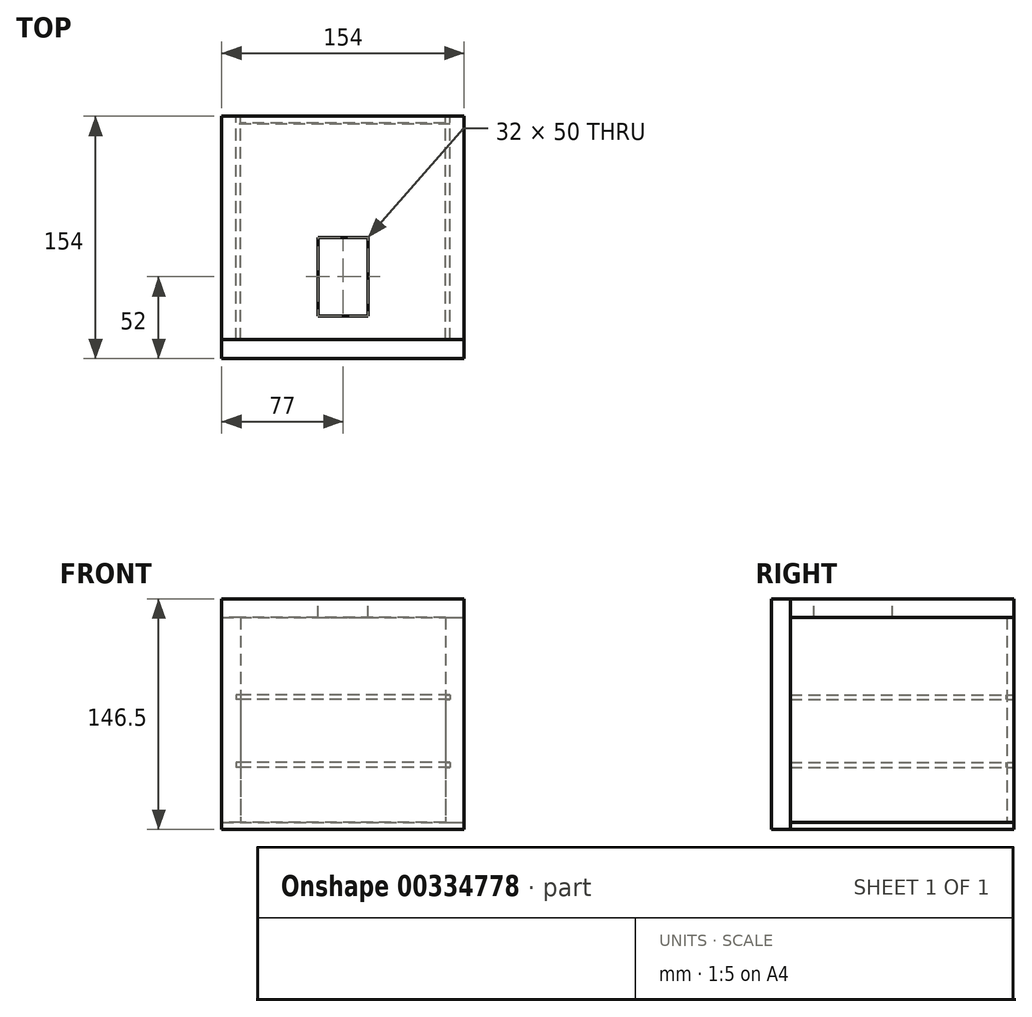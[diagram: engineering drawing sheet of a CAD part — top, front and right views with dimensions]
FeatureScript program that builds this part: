
annotation { "Feature Type Name" : "Feature", "Feature Type Description" : "" }
export const myFeature = defineFeature(function(context is Context, id is Id, definition is map)
    precondition{}
    {
        {
            var Q0;
            Q0=qCreatedBy(makeId("Front.planeOp"),FACE);
            var sketch = newSketch(context, id + "F0", { "sketchPlane" : qUnion([Q0])});
            skLineSegment(sketch, "E0.bottom", {"start": v(-77, 77) * mm, "end": v(77, 77) * mm});
            skLineSegment(sketch, "E0.top", {"start": v(-77, -69.5) * mm, "end": v(77, -69.5) * mm});
            skLineSegment(sketch, "E0.left", {"start": v(-77, 77) * mm, "end": v(-77, -69.5) * mm});
            skLineSegment(sketch, "E0.right", {"start": v(77, 77) * mm, "end": v(77, -69.5) * mm});
            skSolve(sketch);
        }
        {
            var Q0;
            Q0 = qSketchRegion(id + "F0", true);
            var Q1;
            Q1=makeQuery(id+"F0.imprint","IMPRINT",FACE,{"disambiguationData":[TD([[makeQuery(id+"F0.imprint","IMPRINT",EDGE,{"derivedFrom":sQuery(id+"F0.wireOp",EDGE,"E0.bottom")}),-1.0]])]});
            extrude(context, id + "F1", {"entities" : qUnion([Q0, Q1]), "depth" : 12 * mm});
        }
        {
            var Q0;
            Q0=makeQuery(id+"F1.opExtrude","SWEPT_FACE",FACE,{"disambiguationData":[OSD([sQuery(id+"F0.wireOp",EDGE,"E0.right")])]});
            var sketch = newSketch(context, id + "F2", { "sketchPlane" : qUnion([Q0])});
            skLineSegment(sketch, "E1.bottom", {"start": v(0, 65) * mm, "end": v(142, 65) * mm});
            skLineSegment(sketch, "E1.top", {"start": v(0, -65) * mm, "end": v(142, -65) * mm});
            skLineSegment(sketch, "E1.left", {"start": v(0, 65) * mm, "end": v(0, -65) * mm});
            skLineSegment(sketch, "E1.right", {"start": v(142, 65) * mm, "end": v(142, -65) * mm});
            skSolve(sketch);
        }
        {
            var Q0;
            Q0=makeQuery(id+"F2.imprint","IMPRINT",FACE,{"disambiguationData":[TD([[makeQuery(id+"F2.imprint","IMPRINT",EDGE,{"derivedFrom":sQuery(id+"F2.wireOp",EDGE,"E1.bottom")}),-1.0]])]});
            extrude(context, id + "F3", {"entities" : qUnion([Q0]), "oppositeDirection" : true, "depth" : 12 * mm});
        }
        {
            var Q0;
            Q0=makeQuery(id+"F1.opExtrude","SWEPT_BODY",BODY,{"disambiguationData":[OSD([sQuery(id+"F0.wireOp",EDGE,"E0.bottom"),sQuery(id+"F0.wireOp",EDGE,"E0.top"),sQuery(id+"F0.wireOp",EDGE,"E0.left"),sQuery(id+"F0.wireOp",EDGE,"E0.right")])]});
            var Q1;
            Q1=qCreatedBy(makeId("Right.planeOp"),FACE);
            mirror(context, id + "F4", {"entities" : qUnion([Q0]), "mirrorPlane" : qUnion([Q1])});
        }
        {
            var Q0;
            Q0=makeQuery(id+"F1.opExtrude","SWEPT_FACE",FACE,{"disambiguationData":[OSD([sQuery(id+"F0.wireOp",EDGE,"E0.bottom")])]});
            var sketch = newSketch(context, id + "F5", { "sketchPlane" : qUnion([Q0])});
            skLineSegment(sketch, "E2.bottom", {"start": v(77, 0) * mm, "end": v(-77, 0) * mm});
            skLineSegment(sketch, "E2.top", {"start": v(77, 142) * mm, "end": v(-77, 142) * mm});
            skLineSegment(sketch, "E2.left", {"start": v(77, 0) * mm, "end": v(77, 142) * mm});
            skLineSegment(sketch, "E2.right", {"start": v(-77, 0) * mm, "end": v(-77, 142) * mm});
            skLineSegment(sketch, "E3.bottom", {"start": v(-16, 65) * mm, "end": v(16, 65) * mm});
            skLineSegment(sketch, "E3.top", {"start": v(-16, 15) * mm, "end": v(16, 15) * mm});
            skLineSegment(sketch, "E3.left", {"start": v(-16, 65) * mm, "end": v(-16, 15) * mm});
            skLineSegment(sketch, "E3.right", {"start": v(16, 65) * mm, "end": v(16, 15) * mm});
            skSolve(sketch);
        }
        {
            var Q0;
            Q0=makeQuery(id+"F5.imprint","IMPRINT",FACE,{"disambiguationData":[TD([[makeQuery(id+"F5.imprint","IMPRINT",EDGE,{"derivedFrom":sQuery(id+"F5.wireOp",EDGE,"E2.bottom")}),1.0]])]});
            extrude(context, id + "F6", {"entities" : qUnion([Q0]), "oppositeDirection" : true, "depth" : 12 * mm});
        }
        {
            var Q0;
            Q0=makeQuery(id+"F1.opExtrude","SWEPT_FACE",FACE,{"disambiguationData":[OSD([sQuery(id+"F0.wireOp",EDGE,"E0.top")])]});
            var sketch = newSketch(context, id + "F7", { "sketchPlane" : qUnion([Q0])});
            skLineSegment(sketch, "E4.bottom", {"start": v(-77, 0) * mm, "end": v(77, 0) * mm});
            skLineSegment(sketch, "E4.top", {"start": v(-77, -142) * mm, "end": v(77, -142) * mm});
            skLineSegment(sketch, "E4.left", {"start": v(-77, 0) * mm, "end": v(-77, -142) * mm});
            skLineSegment(sketch, "E4.right", {"start": v(77, 0) * mm, "end": v(77, -142) * mm});
            skSolve(sketch);
        }
        {
            var Q0;
            Q0=makeQuery(id+"F7.imprint","IMPRINT",FACE,{"disambiguationData":[TD([[makeQuery(id+"F7.imprint","IMPRINT",EDGE,{"derivedFrom":sQuery(id+"F7.wireOp",EDGE,"E4.bottom")}),-1.0]])]});
            extrude(context, id + "F8", {"entities" : qUnion([Q0]), "oppositeDirection" : true, "depth" : 4.5 * mm});
        }
        {
            var Q0;
            Q0=makeQuery(id+"F4.opPattern","COPY",BODY,{"derivedFrom":makeQuery(id+"F1.opExtrude","SWEPT_BODY",BODY,{"disambiguationData":[OSD([sQuery(id+"F0.wireOp",EDGE,"E0.bottom"),sQuery(id+"F0.wireOp",EDGE,"E0.top"),sQuery(id+"F0.wireOp",EDGE,"E0.left"),sQuery(id+"F0.wireOp",EDGE,"E0.right")])]}),"instanceName":"1"});
            deleteBodies(context, id + "F9", {"entities" : qUnion([Q0])});
        }
        {
            var Q0;
            Q0=makeQuery(id+"F6.opExtrude","SWEPT_FACE",FACE,{"disambiguationData":[OSD([sQuery(id+"F5.wireOp",EDGE,"E2.top")])]});
            var sketch = newSketch(context, id + "F10", { "sketchPlane" : qUnion([Q0])});
            skLineSegment(sketch, "E5.bottom", {"start": v(-65, 65) * mm, "end": v(65, 65) * mm});
            skLineSegment(sketch, "E5.top", {"start": v(-65, -65) * mm, "end": v(65, -65) * mm});
            skLineSegment(sketch, "E5.left", {"start": v(-65, 65) * mm, "end": v(-65, -65) * mm});
            skLineSegment(sketch, "E5.right", {"start": v(65, 65) * mm, "end": v(65, -65) * mm});
            skSolve(sketch);
        }
        {
            var Q0;
            Q0=makeQuery(id+"F10.imprint","IMPRINT",FACE,{"disambiguationData":[TD([[makeQuery(id+"F10.imprint","IMPRINT",EDGE,{"derivedFrom":sQuery(id+"F10.wireOp",EDGE,"E5.bottom")}),-1.0]])]});
            extrude(context, id + "F11", {"entities" : qUnion([Q0]), "oppositeDirection" : true, "depth" : 4.5 * mm});
        }
        {
            var Q0;
            Q0=makeQuery(id+"F3.opExtrude","SWEPT_FACE",FACE,{"disambiguationData":[OSD([sQuery(id+"F2.wireOp",EDGE,"E1.right")])]});
            var sketch = newSketch(context, id + "F12", { "sketchPlane" : qUnion([Q0])});
            skLineSegment(sketch, "E6.bottom", {"start": v(-65, 16) * mm, "end": v(-68, 16) * mm});
            skLineSegment(sketch, "E6.top", {"start": v(-65, 13) * mm, "end": v(-68, 13) * mm});
            skLineSegment(sketch, "E6.left", {"start": v(-65, 16) * mm, "end": v(-65, 13) * mm});
            skLineSegment(sketch, "E6.right", {"start": v(-68, 16) * mm, "end": v(-68, 13) * mm});
            skLineSegment(sketch, "E7.bottom", {"start": v(-65, -27) * mm, "end": v(-68, -27) * mm});
            skLineSegment(sketch, "E7.top", {"start": v(-65, -30) * mm, "end": v(-68, -30) * mm});
            skLineSegment(sketch, "E7.left", {"start": v(-65, -27) * mm, "end": v(-65, -30) * mm});
            skLineSegment(sketch, "E7.right", {"start": v(-68, -27) * mm, "end": v(-68, -30) * mm});
            skSolve(sketch);
        }
        {
            var Q0;
            Q0=makeQuery(id+"F12.imprint","IMPRINT",FACE,{"disambiguationData":[TD([[makeQuery(id+"F12.imprint","IMPRINT",EDGE,{"derivedFrom":sQuery(id+"F12.wireOp",EDGE,"NvQbIwnB-lqE2-p2Xs-orIO-Tnx0DaEzGyps.bottom")}),1.0]])]});
            var Q1;
            Q1=makeQuery(id+"F12.imprint","IMPRINT",FACE,{"disambiguationData":[TD([[makeQuery(id+"F12.imprint","IMPRINT",EDGE,{"derivedFrom":sQuery(id+"F12.wireOp",EDGE,"E6.bottom")}),1.0]])]});
            var Q2;
            Q2=makeQuery(id+"F12.imprint","IMPRINT",FACE,{"disambiguationData":[TD([[makeQuery(id+"F12.imprint","IMPRINT",EDGE,{"derivedFrom":sQuery(id+"F12.wireOp",EDGE,"E7.bottom")}),1.0]])]});
            extrude(context, id + "F13", {"entities" : qUnion([Q0, Q1, Q2]), "operationType" : NewBodyOperationType.REMOVE, "oppositeDirection" : true, "depth" : 142 * mm});
        }
        {
            var Q0;
            Q0=makeQuery(id+"F3.opExtrude","SWEPT_BODY",BODY,{"disambiguationData":[OSD([sQuery(id+"F2.wireOp",EDGE,"E1.bottom"),sQuery(id+"F2.wireOp",EDGE,"E1.top"),sQuery(id+"F2.wireOp",EDGE,"E1.left"),sQuery(id+"F2.wireOp",EDGE,"E1.right")])]});
            var Q1;
            Q1=qCreatedBy(makeId("Right.planeOp"),FACE);
            mirror(context, id + "F14", {"entities" : qUnion([Q0]), "mirrorPlane" : qUnion([Q1])});
        }
        {
            var Q0;
            Q0=makeQuery(id+"F13.boolean.opBoolean","COPY",FACE,{"derivedFrom":makeQuery(id+"F13.opExtrude","SWEPT_FACE",FACE,{"disambiguationData":[OSD([sQuery(id+"F12.wireOp",EDGE,"E6.top")])]})});
            var sketch = newSketch(context, id + "F15", { "sketchPlane" : qUnion([Q0])});
            skLineSegment(sketch, "E8.bottom", {"start": v(68, 0) * mm, "end": v(-68, 0) * mm});
            skLineSegment(sketch, "E8.top", {"start": v(68, 137) * mm, "end": v(-68, 137) * mm});
            skLineSegment(sketch, "E8.left", {"start": v(68, 0) * mm, "end": v(68, 137) * mm});
            skLineSegment(sketch, "E8.right", {"start": v(-68, 0) * mm, "end": v(-68, 137) * mm});
            skSolve(sketch);
        }
        {
            var Q0;
            Q0 = qSketchRegion(id + "F15", true);
            extrude(context, id + "F16", {"entities" : qUnion([Q0]), "depth" : 3 * mm});
        }
        {
            var Q0;
            Q0=makeQuery(id+"F16.opExtrude","SWEPT_BODY",BODY,{"disambiguationData":[OSD([sQuery(id+"F15.wireOp",EDGE,"E8.bottom"),sQuery(id+"F15.wireOp",EDGE,"E8.top"),sQuery(id+"F15.wireOp",EDGE,"E8.left"),sQuery(id+"F15.wireOp",EDGE,"E8.right")])]});
            transform(context, id + "F17", {"entities" : qUnion([Q0]), "transformType" : TransformType.TRANSLATION_3D, "dx" : 0 * mm, "dy" : 0 * mm, "dz" : -43 * mm, "makeCopy" : true});
        }
    });
